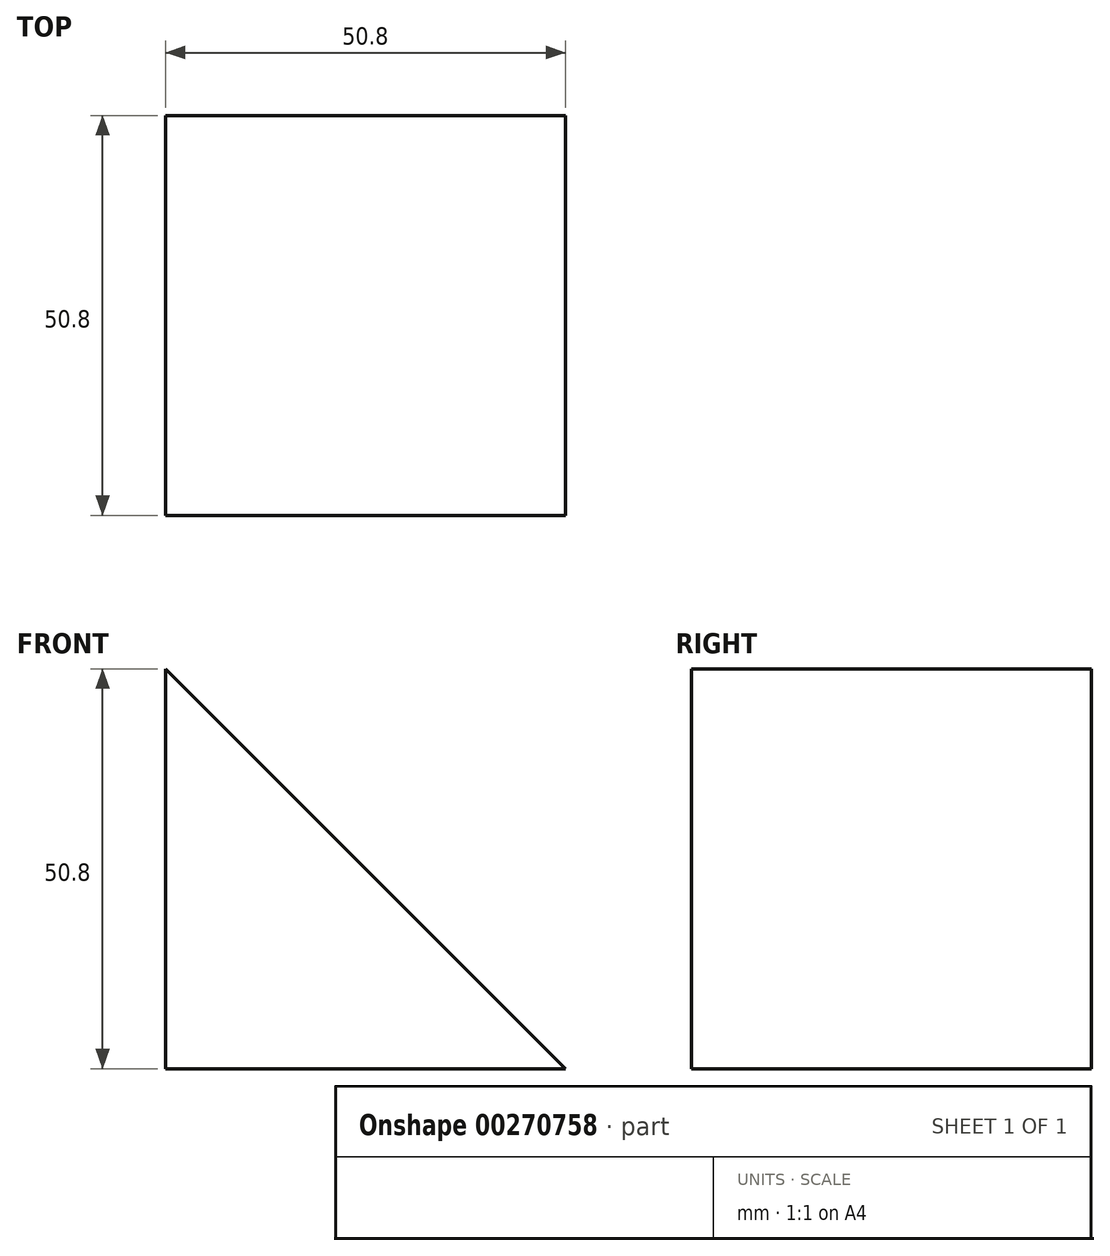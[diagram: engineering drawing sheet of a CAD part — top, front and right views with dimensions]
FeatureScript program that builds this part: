
annotation { "Feature Type Name" : "Feature", "Feature Type Description" : "" }
export const myFeature = defineFeature(function(context is Context, id is Id, definition is map)
    precondition{}
    {
        {
            var Q0;
            Q0=qCreatedBy(makeId("Front.planeOp"),FACE);
            var sketch = newSketch(context, id + "F0", { "sketchPlane" : qUnion([Q0])});
            skLineSegment(sketch, "E0.bottom", {"start": v(0, 0) * mm, "end": v(-50.8, 0) * mm});
            skLineSegment(sketch, "E0.top", {"start": v(0, 50.8) * mm, "end": v(-50.8, 50.8) * mm});
            skLineSegment(sketch, "E0.left", {"start": v(0, 0) * mm, "end": v(0, 50.8) * mm});
            skLineSegment(sketch, "E0.right", {"start": v(-50.8, 0) * mm, "end": v(-50.8, 50.8) * mm});
            skSolve(sketch);
        }
        {
            var Q0;
            Q0=makeQuery(id+"F0.imprint","IMPRINT",FACE,{"disambiguationData":[TD([[makeQuery(id+"F0.imprint","IMPRINT",EDGE,{"derivedFrom":sQuery(id+"F0.wireOp",EDGE,"E0.bottom")}),-1.0]])]});
            extrude(context, id + "F1", {"entities" : qUnion([Q0]), "depth" : 50.8 * mm});
        }
        {
            var Q0;
            Q0=makeQuery(id+"F1.opExtrude","CAP_FACE",FACE,{"disambiguationData":[OSD([sQuery(id+"F0.wireOp",EDGE,"E0.bottom"),sQuery(id+"F0.wireOp",EDGE,"E0.top"),sQuery(id+"F0.wireOp",EDGE,"E0.left"),sQuery(id+"F0.wireOp",EDGE,"E0.right")])],"isStart":false});
            var sketch = newSketch(context, id + "F2", { "sketchPlane" : qUnion([Q0])});
            skLineSegment(sketch, "E1", {"start": v(-50.8, 50.8) * mm, "end": v(0, 0) * mm});
            skSolve(sketch);
        }
        {
            var Q0;
            Q0=makeQuery(id+"F2.imprint","IMPRINT",FACE,{"disambiguationData":[TD([[makeQuery(id+"F2.imprint","IMPRINT",EDGE,{"derivedFrom":sQuery(id+"F2.wireOp",EDGE,"E1")}),1.0]])]});
            extrude(context, id + "F3", {"entities" : qUnion([Q0]), "operationType" : NewBodyOperationType.REMOVE, "oppositeDirection" : true, "depth" : 50.8 * mm});
        }
    });
